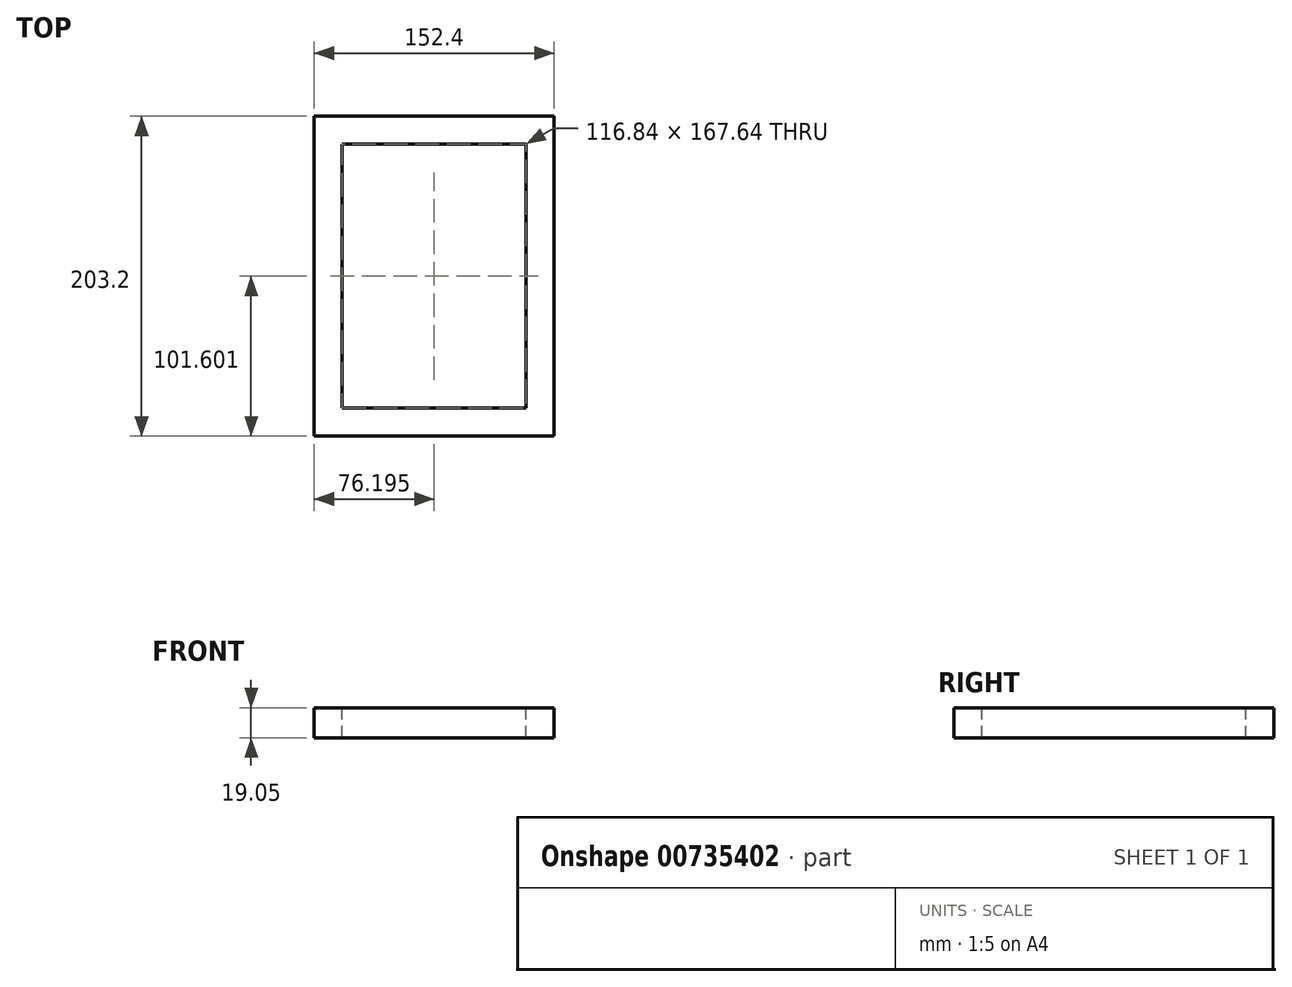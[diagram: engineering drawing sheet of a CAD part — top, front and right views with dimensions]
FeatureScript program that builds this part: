
annotation { "Feature Type Name" : "Feature", "Feature Type Description" : "" }
export const myFeature = defineFeature(function(context is Context, id is Id, definition is map)
    precondition{}
    {
        {
            var Q0;
            Q0=qCreatedBy(makeId("Top.planeOp"),FACE);
            var sketch = newSketch(context, id + "F0", { "sketchPlane" : qUnion([Q0])});
            skLineSegment(sketch, "E0.bottom", {"start": v(-96.66, 102.21) * mm, "end": v(55.74, 102.21) * mm});
            skLineSegment(sketch, "E0.top", {"start": v(-96.66, -100.99) * mm, "end": v(55.74, -100.99) * mm});
            skLineSegment(sketch, "E0.left", {"start": v(-96.66, 102.21) * mm, "end": v(-96.66, -100.99) * mm});
            skLineSegment(sketch, "E0.right", {"start": v(55.74, 102.21) * mm, "end": v(55.74, -100.99) * mm});
            skSolve(sketch);
        }
        {
            var Q0;
            Q0=makeQuery(id+"F0.imprint","IMPRINT",FACE,{"disambiguationData":[TD([[makeQuery(id+"F0.imprint","IMPRINT",EDGE,{"derivedFrom":sQuery(id+"F0.wireOp",EDGE,"E0.bottom")}),-1.0]])]});
            extrude(context, id + "F1", {"entities" : qUnion([Q0]), "depth" : 19.05 * mm, "offsetDistance" : 25.4 * mm});
        }
        {
            var Q0;
            Q0=makeQuery(id+"F1.opExtrude","CAP_FACE",FACE,{"disambiguationData":[OSD([sQuery(id+"F0.wireOp",EDGE,"E0.bottom"),sQuery(id+"F0.wireOp",EDGE,"E0.top"),sQuery(id+"F0.wireOp",EDGE,"E0.left"),sQuery(id+"F0.wireOp",EDGE,"E0.right")])],"isStart":false});
            var sketch = newSketch(context, id + "F2", { "sketchPlane" : qUnion([Q0])});
            skLineSegment(sketch, "E1.0", {"start": v(-78.88, 84.43) * mm, "end": v(-78.88, -83.2) * mm});
            skLineSegment(sketch, "E1.1", {"start": v(37.96, 84.43) * mm, "end": v(-78.88, 84.43) * mm});
            skLineSegment(sketch, "E1.2", {"start": v(37.96, -83.2) * mm, "end": v(37.96, 84.43) * mm});
            skLineSegment(sketch, "E1.3", {"start": v(-78.88, -83.2) * mm, "end": v(37.96, -83.2) * mm});
            skSolve(sketch);
        }
        {
            var Q0;
            Q0=makeQuery(id+"F2.imprint","IMPRINT",FACE,{"disambiguationData":[TD([[makeQuery(id+"F2.imprint","IMPRINT",EDGE,{"derivedFrom":sQuery(id+"F2.wireOp",EDGE,"E1.0")}),1.0]])]});
            extrude(context, id + "F3", {"entities" : qUnion([Q0]), "operationType" : NewBodyOperationType.REMOVE, "oppositeDirection" : true, "depth" : 25.4 * mm, "offsetDistance" : 25.4 * mm});
        }
    });
